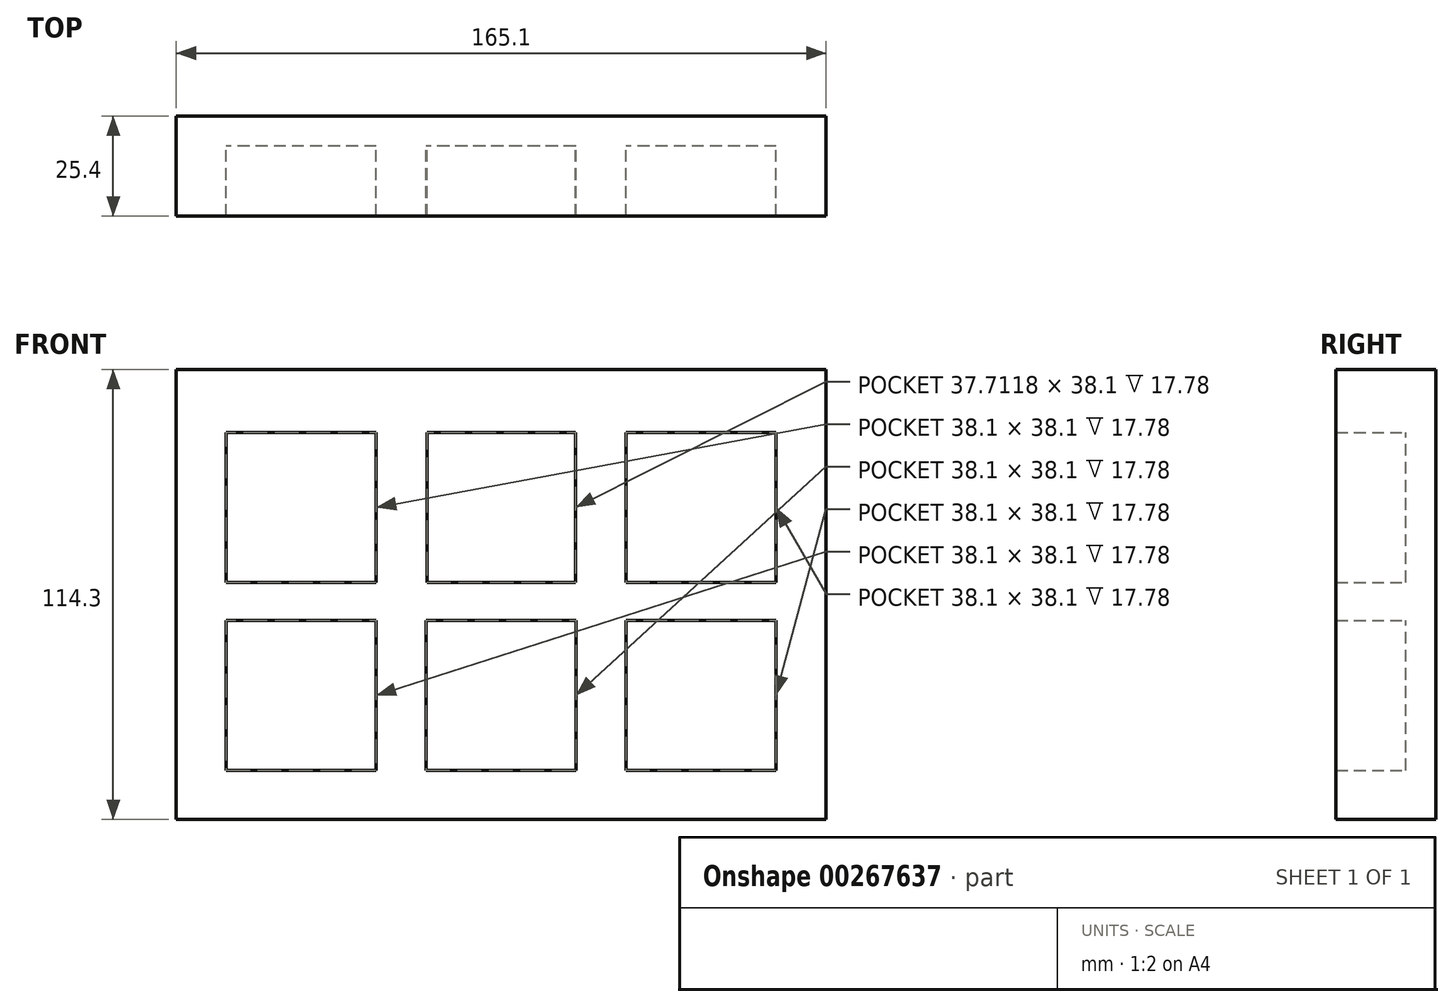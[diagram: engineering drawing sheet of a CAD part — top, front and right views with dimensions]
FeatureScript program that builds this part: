
annotation { "Feature Type Name" : "Feature", "Feature Type Description" : "" }
export const myFeature = defineFeature(function(context is Context, id is Id, definition is map)
    precondition{}
    {
        {
            var Q0;
            Q0=qCreatedBy(makeId("Front.planeOp"),FACE);
            var sketch = newSketch(context, id + "F0", { "sketchPlane" : qUnion([Q0])});
            skLineSegment(sketch, "E0.bottom", {"start": v(82.55, -57.15) * mm, "end": v(-82.55, -57.15) * mm});
            skLineSegment(sketch, "E0.top", {"start": v(82.55, 57.15) * mm, "end": v(-82.55, 57.15) * mm});
            skLineSegment(sketch, "E0.left", {"start": v(82.55, -57.15) * mm, "end": v(82.55, 57.15) * mm});
            skLineSegment(sketch, "E0.right", {"start": v(-82.55, -57.15) * mm, "end": v(-82.55, 57.15) * mm});
            skPoint(sketch, "E0.middle", {"position": v(0, 0) * mm});
            skPoint(sketch, "E1", {"position": v(0, 22.14) * mm});
            skPoint(sketch, "E2", {"position": v(0, -25.62) * mm});
            skPoint(sketch, "E3", {"position": v(-50.8, 22.14) * mm});
            skPoint(sketch, "E4", {"position": v(50.8, 22.14) * mm});
            skPoint(sketch, "E5", {"position": v(50.8, -25.62) * mm});
            skPoint(sketch, "E6", {"position": v(-50.8, -25.62) * mm});
            skLineSegment(sketch, "E7.bottom", {"start": v(18.86, 3.1) * mm, "end": v(-18.86, 3.1) * mm});
            skLineSegment(sketch, "E7.top", {"start": v(18.86, 41.2) * mm, "end": v(-18.86, 41.2) * mm});
            skLineSegment(sketch, "E7.left", {"start": v(18.86, 3.1) * mm, "end": v(18.86, 41.2) * mm});
            skLineSegment(sketch, "E7.right", {"start": v(-18.86, 3.1) * mm, "end": v(-18.86, 41.2) * mm});
            skLineSegment(sketch, "E8.bottom", {"start": v(-31.75, 3.1) * mm, "end": v(-69.85, 3.1) * mm});
            skLineSegment(sketch, "E8.top", {"start": v(-31.75, 41.2) * mm, "end": v(-69.85, 41.2) * mm});
            skLineSegment(sketch, "E8.left", {"start": v(-31.75, 3.1) * mm, "end": v(-31.75, 41.2) * mm});
            skLineSegment(sketch, "E8.right", {"start": v(-69.85, 3.1) * mm, "end": v(-69.85, 41.2) * mm});
            skLineSegment(sketch, "E9.bottom", {"start": v(19.05, -44.67) * mm, "end": v(-19.05, -44.67) * mm});
            skLineSegment(sketch, "E9.top", {"start": v(19.05, -6.57) * mm, "end": v(-19.05, -6.57) * mm});
            skLineSegment(sketch, "E9.left", {"start": v(19.05, -44.67) * mm, "end": v(19.05, -6.57) * mm});
            skLineSegment(sketch, "E9.right", {"start": v(-19.05, -44.67) * mm, "end": v(-19.05, -6.57) * mm});
            skLineSegment(sketch, "E10.bottom", {"start": v(69.85, -44.67) * mm, "end": v(31.75, -44.67) * mm});
            skLineSegment(sketch, "E10.top", {"start": v(69.85, -6.57) * mm, "end": v(31.75, -6.57) * mm});
            skLineSegment(sketch, "E10.left", {"start": v(69.85, -44.67) * mm, "end": v(69.85, -6.57) * mm});
            skLineSegment(sketch, "E10.right", {"start": v(31.75, -44.67) * mm, "end": v(31.75, -6.57) * mm});
            skLineSegment(sketch, "E11.bottom", {"start": v(-31.75, -44.67) * mm, "end": v(-69.85, -44.67) * mm});
            skLineSegment(sketch, "E11.top", {"start": v(-31.75, -6.57) * mm, "end": v(-69.85, -6.57) * mm});
            skLineSegment(sketch, "E11.left", {"start": v(-31.75, -44.67) * mm, "end": v(-31.75, -6.57) * mm});
            skLineSegment(sketch, "E11.right", {"start": v(-69.85, -44.67) * mm, "end": v(-69.85, -6.57) * mm});
            skLineSegment(sketch, "E12.bottom", {"start": v(69.85, 3.1) * mm, "end": v(31.75, 3.1) * mm});
            skLineSegment(sketch, "E12.top", {"start": v(69.85, 41.2) * mm, "end": v(31.75, 41.2) * mm});
            skLineSegment(sketch, "E12.left", {"start": v(69.85, 3.1) * mm, "end": v(69.85, 41.2) * mm});
            skLineSegment(sketch, "E12.right", {"start": v(31.75, 3.1) * mm, "end": v(31.75, 41.2) * mm});
            skSolve(sketch);
        }
        {
            var Q0;
            Q0=makeQuery(id+"F0.imprint","IMPRINT",FACE,{"disambiguationData":[TD([[makeQuery(id+"F0.imprint","IMPRINT",EDGE,{"derivedFrom":sQuery(id+"F0.wireOp",EDGE,"E0.bottom")}),-1.0]])]});
            extrude(context, id + "F1", {"entities" : qUnion([Q0]), "depth" : 25.4 * mm});
        }
        {
            var Q0;
            Q0=makeQuery(id+"F0.imprint","IMPRINT",FACE,{"disambiguationData":[TD([[makeQuery(id+"F0.imprint","IMPRINT",EDGE,{"derivedFrom":sQuery(id+"F0.wireOp",EDGE,"E8.bottom")}),-1.0]])]});
            var Q1;
            Q1=makeQuery(id+"F0.imprint","IMPRINT",FACE,{"disambiguationData":[TD([[makeQuery(id+"F0.imprint","IMPRINT",EDGE,{"derivedFrom":sQuery(id+"F0.wireOp",EDGE,"E7.bottom")}),-1.0]])]});
            var Q2;
            Q2=makeQuery(id+"F0.imprint","IMPRINT",FACE,{"disambiguationData":[TD([[makeQuery(id+"F0.imprint","IMPRINT",EDGE,{"derivedFrom":sQuery(id+"F0.wireOp",EDGE,"E12.bottom")}),-1.0]])]});
            var Q3;
            Q3=makeQuery(id+"F0.imprint","IMPRINT",FACE,{"disambiguationData":[TD([[makeQuery(id+"F0.imprint","IMPRINT",EDGE,{"derivedFrom":sQuery(id+"F0.wireOp",EDGE,"E11.bottom")}),-1.0]])]});
            var Q4;
            Q4=makeQuery(id+"F0.imprint","IMPRINT",FACE,{"disambiguationData":[TD([[makeQuery(id+"F0.imprint","IMPRINT",EDGE,{"derivedFrom":sQuery(id+"F0.wireOp",EDGE,"E9.bottom")}),-1.0]])]});
            var Q5;
            Q5=makeQuery(id+"F0.imprint","IMPRINT",FACE,{"disambiguationData":[TD([[makeQuery(id+"F0.imprint","IMPRINT",EDGE,{"derivedFrom":sQuery(id+"F0.wireOp",EDGE,"E10.bottom")}),-1.0]])]});
            extrude(context, id + "F2", {"entities" : qUnion([Q0, Q1, Q2, Q3, Q4, Q5]), "operationType" : NewBodyOperationType.ADD, "depth" : 7.62 * mm});
        }
    });
